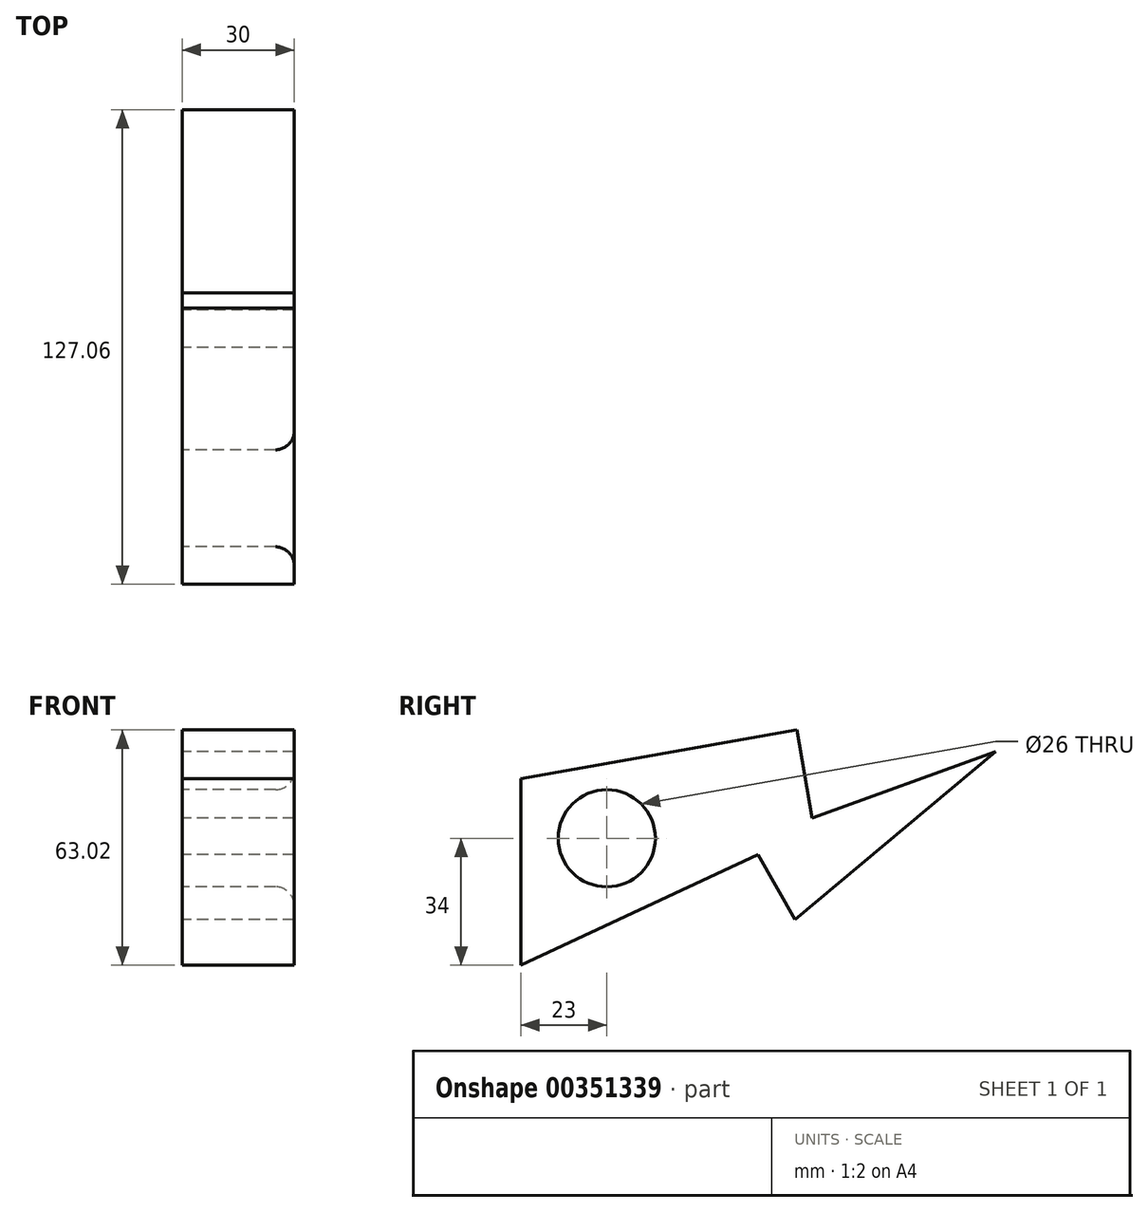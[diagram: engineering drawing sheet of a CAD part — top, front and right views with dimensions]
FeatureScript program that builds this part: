
annotation { "Feature Type Name" : "Feature", "Feature Type Description" : "" }
export const myFeature = defineFeature(function(context is Context, id is Id, definition is map)
    precondition{}
    {
        {
            var Q0;
            Q0=qCreatedBy(makeId("Right.planeOp"),FACE);
            var sketch = newSketch(context, id + "F0", { "sketchPlane" : qUnion([Q0])});
            skLineSegment(sketch, "E0", {"start": v(0, 0) * mm, "end": v(0, 50) * mm});
            skLineSegment(sketch, "E1", {"start": v(0, 50) * mm, "end": v(73.86, 63.02) * mm});
            skLineSegment(sketch, "E2", {"start": v(73.86, 63.02) * mm, "end": v(78.02, 39.4) * mm});
            skLineSegment(sketch, "E3", {"start": v(78.02, 39.4) * mm, "end": v(127.06, 57.26) * mm});
            skLineSegment(sketch, "E4", {"start": v(127.06, 57.26) * mm, "end": v(73.44, 12.26) * mm});
            skLineSegment(sketch, "E5", {"start": v(73.44, 12.26) * mm, "end": v(63.44, 29.58) * mm});
            skLineSegment(sketch, "E6", {"start": v(63.44, 29.58) * mm, "end": v(0, 0) * mm});
            skCircle(sketch, "E7", {"center": v(23, 34) * mm, "radius": 13 * mm});
            skSolve(sketch);
        }
        {
            var Q0;
            Q0=makeQuery(id+"F0.imprint","IMPRINT",FACE,{"disambiguationData":[TD([[makeQuery(id+"F0.imprint","IMPRINT",EDGE,{"derivedFrom":sQuery(id+"F0.wireOp",EDGE,"E0")}),-1.0]])]});
            extrude(context, id + "F1", {"entities" : qUnion([Q0]), "depth" : 30 * mm});
        }
        {
            var Q0;
            Q0=makeQuery(id+"F1.opExtrude","CAP_EDGE",EDGE,{"disambiguationData":[OSD([sQuery(id+"F0.wireOp",EDGE,"E7")])],"isStart":false});
            fillet(context, id + "F2", {"entities" : qUnion([Q0]), "radius" : 5 * mm, "tangentPropagation" : true, "allowEdgeOverflow" : false});
        }
    });
